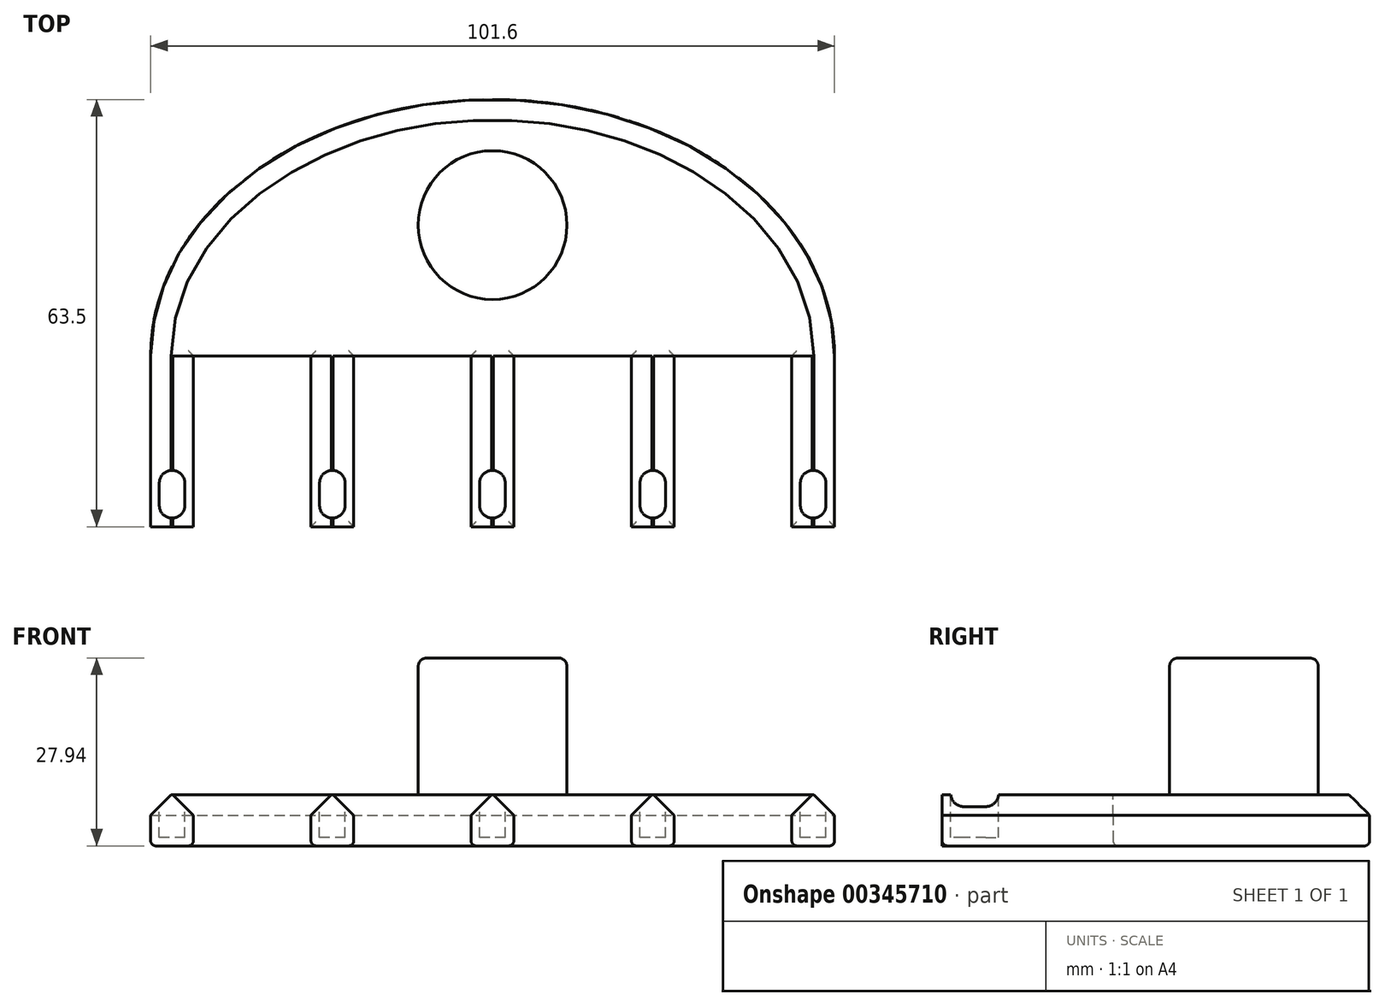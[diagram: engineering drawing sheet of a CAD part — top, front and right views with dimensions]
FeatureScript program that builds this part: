
annotation { "Feature Type Name" : "Feature", "Feature Type Description" : "" }
export const myFeature = defineFeature(function(context is Context, id is Id, definition is map)
    precondition{}
    {
        {
            var Q0;
            Q0=qCreatedBy(makeId("Top.planeOp"),FACE);
            var sketch = newSketch(context, id + "F0", { "sketchPlane" : qUnion([Q0])});
            skEllipticalArc(sketch, "E0", {});
            skPoint(sketch, "E1.end.orphan", {"position": v(-50.8, 0) * mm});
            skPoint(sketch, "E1.start.orphan", {"position": v(50.8, 0) * mm});
            skLineSegment(sketch, "E2", {"start": v(-50.8, 0) * mm, "end": v(-50.8, -25.4) * mm});
            skLineSegment(sketch, "E3", {"start": v(-50.8, -25.4) * mm, "end": v(-44.45, -25.4) * mm});
            skLineSegment(sketch, "E4", {"start": v(-44.45, -25.4) * mm, "end": v(-44.45, 0) * mm});
            skLineSegment(sketch, "E5", {"start": v(-44.45, 0) * mm, "end": v(-26.99, 0) * mm});
            skLineSegment(sketch, "E6", {"start": v(-26.99, 0) * mm, "end": v(-26.99, -25.4) * mm});
            skLineSegment(sketch, "E7", {"start": v(-26.99, -25.4) * mm, "end": v(-20.64, -25.4) * mm});
            skLineSegment(sketch, "E8", {"start": v(-20.64, -25.4) * mm, "end": v(-20.64, 0) * mm});
            skLineSegment(sketch, "E9", {"start": v(-20.64, 0) * mm, "end": v(-3.2, 0) * mm});
            skLineSegment(sketch, "E10", {"start": v(-3.2, 0) * mm, "end": v(-3.2, -25.4) * mm});
            skLineSegment(sketch, "E11", {"start": v(-3.2, -25.4) * mm, "end": v(3.15, -25.4) * mm});
            skLineSegment(sketch, "E12", {"start": v(3.15, -25.4) * mm, "end": v(3.15, 0) * mm});
            skLineSegment(sketch, "E13", {"start": v(3.15, 0) * mm, "end": v(20.62, 0) * mm});
            skLineSegment(sketch, "E14", {"start": v(20.62, 0) * mm, "end": v(20.62, -25.4) * mm});
            skLineSegment(sketch, "E15", {"start": v(20.62, -25.4) * mm, "end": v(26.97, -25.4) * mm});
            skLineSegment(sketch, "E16", {"start": v(26.97, -25.4) * mm, "end": v(26.97, 0) * mm});
            skLineSegment(sketch, "E17", {"start": v(26.97, 0) * mm, "end": v(44.45, 0) * mm});
            skLineSegment(sketch, "E18", {"start": v(44.45, 0) * mm, "end": v(44.45, -25.4) * mm});
            skLineSegment(sketch, "E19", {"start": v(44.45, -25.4) * mm, "end": v(50.8, -25.4) * mm});
            skLineSegment(sketch, "E20", {"start": v(50.8, -25.4) * mm, "end": v(50.8, 0) * mm});
            const initialGuessF0  = {"E0": [0, 0, 1, 0, 0.0508, 0.0381, 0, 3.141592653589793]};
            skSetInitialGuess(sketch, initialGuessF0);
            skSolve(sketch);
        }
        {
            var Q0;
            Q0=makeQuery(id+"F0.imprint","IMPRINT",FACE,{"disambiguationData":[TD([[makeQuery(id+"F0.imprint","IMPRINT",EDGE,{"derivedFrom":sQuery(id+"F0.wireOp",EDGE,"E0")}),1.0]])]});
            extrude(context, id + "F1", {"entities" : qUnion([Q0]), "depth" : 7.62 * mm});
        }
        {
            var Q0;
            Q0=makeQuery(id+"F1.opExtrude","CAP_FACE",FACE,{"disambiguationData":[OSD([sQuery(id+"F0.wireOp",EDGE,"E0"),sQuery(id+"F0.wireOp",EDGE,"soE1Z759-kknB-JbUd-iDBq-yKROK0KpcBBy")])],"isStart":false});
            var sketch = newSketch(context, id + "F2", { "sketchPlane" : qUnion([Q0])});
            skCircle(sketch, "E21", {"center": v(0, 19.43) * mm, "radius": 11.05 * mm});
            skSolve(sketch);
        }
        {
            var Q0;
            Q0=makeQuery(id+"F2.imprint","IMPRINT",FACE,{"disambiguationData":[TD([[makeQuery(id+"F2.imprint","IMPRINT",EDGE,{"derivedFrom":sQuery(id+"F2.wireOp",EDGE,"E21")}),1.0]])]});
            extrude(context, id + "F3", {"entities" : qUnion([Q0]), "operationType" : NewBodyOperationType.ADD, "depth" : 20.32 * mm});
        }
        {
            var Q0;
            Q0=makeQuery(id+"F1.opExtrude","CAP_FACE",FACE,{"disambiguationData":[OSD([sQuery(id+"F0.wireOp",EDGE,"E0"),sQuery(id+"F0.wireOp",EDGE,"E2"),sQuery(id+"F0.wireOp",EDGE,"E3"),sQuery(id+"F0.wireOp",EDGE,"E4"),sQuery(id+"F0.wireOp",EDGE,"E5"),sQuery(id+"F0.wireOp",EDGE,"E6"),sQuery(id+"F0.wireOp",EDGE,"E7"),sQuery(id+"F0.wireOp",EDGE,"E8"),sQuery(id+"F0.wireOp",EDGE,"E9"),sQuery(id+"F0.wireOp",EDGE,"E10"),sQuery(id+"F0.wireOp",EDGE,"E11"),sQuery(id+"F0.wireOp",EDGE,"E12"),sQuery(id+"F0.wireOp",EDGE,"E13"),sQuery(id+"F0.wireOp",EDGE,"E14"),sQuery(id+"F0.wireOp",EDGE,"E15"),sQuery(id+"F0.wireOp",EDGE,"E16"),sQuery(id+"F0.wireOp",EDGE,"E17"),sQuery(id+"F0.wireOp",EDGE,"E18"),sQuery(id+"F0.wireOp",EDGE,"E19"),sQuery(id+"F0.wireOp",EDGE,"E20")])],"isStart":false});
            var sketch = newSketch(context, id + "F4", { "sketchPlane" : qUnion([Q0])});
            skLineSegment(sketch, "E22", {"start": v(-49.53, -18.92) * mm, "end": v(-49.53, -22.23) * mm});
            skArc(sketch, "E23", {"start": v(-49.53, -22.23) * mm, "mid": v(-47.63, -24.13) * mm, "end": v(-45.72, -22.23) * mm});
            skLineSegment(sketch, "E24", {"start": v(-45.72, -22.23) * mm, "end": v(-45.72, -18.92) * mm});
            skArc(sketch, "E25", {"start": v(-49.53, -18.92) * mm, "mid": v(-47.63, -17.02) * mm, "end": v(-45.72, -18.92) * mm});
            skLineSegment(sketch, "E26", {"start": v(-25.72, -18.92) * mm, "end": v(-25.72, -22.23) * mm});
            skArc(sketch, "E27", {"start": v(-25.72, -22.23) * mm, "mid": v(-23.81, -24.13) * mm, "end": v(-21.9, -22.23) * mm});
            skLineSegment(sketch, "E28", {"start": v(-21.9, -22.23) * mm, "end": v(-21.9, -18.92) * mm});
            skArc(sketch, "E29", {"start": v(-25.72, -18.92) * mm, "mid": v(-23.81, -17.02) * mm, "end": v(-21.9, -18.92) * mm});
            skLineSegment(sketch, "E30", {"start": v(-1.93, -18.92) * mm, "end": v(-1.93, -22.23) * mm});
            skArc(sketch, "E31", {"start": v(-1.93, -22.23) * mm, "mid": v(-0.03, -24.13) * mm, "end": v(1.88, -22.23) * mm});
            skLineSegment(sketch, "E32", {"start": v(1.88, -22.23) * mm, "end": v(1.88, -18.92) * mm});
            skArc(sketch, "E33", {"start": v(-1.93, -18.92) * mm, "mid": v(-0.03, -17.02) * mm, "end": v(1.88, -18.92) * mm});
            skLineSegment(sketch, "E34", {"start": v(21.9, -18.92) * mm, "end": v(21.9, -22.23) * mm});
            skArc(sketch, "E35", {"start": v(21.9, -22.23) * mm, "mid": v(23.8, -24.13) * mm, "end": v(25.7, -22.23) * mm});
            skLineSegment(sketch, "E36", {"start": v(25.7, -22.23) * mm, "end": v(25.7, -18.92) * mm});
            skArc(sketch, "E37", {"start": v(21.9, -18.92) * mm, "mid": v(23.8, -17.02) * mm, "end": v(25.7, -18.92) * mm});
            skLineSegment(sketch, "E38", {"start": v(45.72, -18.92) * mm, "end": v(45.72, -22.22) * mm});
            skArc(sketch, "E39", {"start": v(45.72, -22.22) * mm, "mid": v(47.62, -24.13) * mm, "end": v(49.53, -22.22) * mm});
            skLineSegment(sketch, "E40", {"start": v(49.53, -22.22) * mm, "end": v(49.53, -18.92) * mm});
            skArc(sketch, "E41", {"start": v(45.72, -18.92) * mm, "mid": v(47.62, -17.02) * mm, "end": v(49.53, -18.92) * mm});
            skSolve(sketch);
        }
        {
            var Q0;
            Q0=makeQuery(id+"F4.imprint","IMPRINT",FACE,{"disambiguationData":[TD([[makeQuery(id+"F4.imprint","IMPRINT",EDGE,{"derivedFrom":sQuery(id+"F4.wireOp",EDGE,"E30")}),1.0]])]});
            var Q1;
            Q1=makeQuery(id+"F4.imprint","IMPRINT",FACE,{"disambiguationData":[TD([[makeQuery(id+"F4.imprint","IMPRINT",EDGE,{"derivedFrom":sQuery(id+"F4.wireOp",EDGE,"E34")}),1.0]])]});
            var Q2;
            Q2=makeQuery(id+"F4.imprint","IMPRINT",FACE,{"disambiguationData":[TD([[makeQuery(id+"F4.imprint","IMPRINT",EDGE,{"derivedFrom":sQuery(id+"F4.wireOp",EDGE,"E38")}),1.0]])]});
            var Q3;
            Q3=makeQuery(id+"F4.imprint","IMPRINT",FACE,{"disambiguationData":[TD([[makeQuery(id+"F4.imprint","IMPRINT",EDGE,{"derivedFrom":sQuery(id+"F4.wireOp",EDGE,"E26")}),1.0]])]});
            var Q4;
            Q4=makeQuery(id+"F4.imprint","IMPRINT",FACE,{"disambiguationData":[TD([[makeQuery(id+"F4.imprint","IMPRINT",EDGE,{"derivedFrom":sQuery(id+"F4.wireOp",EDGE,"E22")}),1.0]])]});
            extrude(context, id + "F5", {"entities" : qUnion([Q0, Q1, Q2, Q3, Q4]), "operationType" : NewBodyOperationType.REMOVE, "oppositeDirection" : true, "depth" : 6.35 * mm});
        }
        {
            var Q0;
            Q0=makeQuery(id+"F1.opExtrude","CAP_EDGE",EDGE,{"disambiguationData":[OSD([sQuery(id+"F0.wireOp",EDGE,"E2")])],"isStart":false});
            var Q1;
            Q1=makeQuery(id+"F1.opExtrude","CAP_EDGE",EDGE,{"disambiguationData":[OSD([sQuery(id+"F0.wireOp",EDGE,"E4")])],"isStart":false});
            var Q2;
            Q2=makeQuery(id+"F1.opExtrude","CAP_EDGE",EDGE,{"disambiguationData":[OSD([sQuery(id+"F0.wireOp",EDGE,"E6")])],"isStart":false});
            var Q3;
            Q3=makeQuery(id+"F1.opExtrude","CAP_EDGE",EDGE,{"disambiguationData":[OSD([sQuery(id+"F0.wireOp",EDGE,"E8")])],"isStart":false});
            var Q4;
            Q4=makeQuery(id+"F1.opExtrude","CAP_EDGE",EDGE,{"disambiguationData":[OSD([sQuery(id+"F0.wireOp",EDGE,"E10")])],"isStart":false});
            var Q5;
            Q5=makeQuery(id+"F1.opExtrude","CAP_EDGE",EDGE,{"disambiguationData":[OSD([sQuery(id+"F0.wireOp",EDGE,"E12")])],"isStart":false});
            var Q6;
            Q6=makeQuery(id+"F1.opExtrude","CAP_EDGE",EDGE,{"disambiguationData":[OSD([sQuery(id+"F0.wireOp",EDGE,"E14")])],"isStart":false});
            var Q7;
            Q7=makeQuery(id+"F1.opExtrude","CAP_EDGE",EDGE,{"disambiguationData":[OSD([sQuery(id+"F0.wireOp",EDGE,"E16")])],"isStart":false});
            var Q8;
            Q8=makeQuery(id+"F1.opExtrude","CAP_EDGE",EDGE,{"disambiguationData":[OSD([sQuery(id+"F0.wireOp",EDGE,"E18")])],"isStart":false});
            chamfer(context, id + "F6", {"entities" : qUnion([Q0, Q1, Q2, Q3, Q4, Q5, Q6, Q7, Q8]), "width" : 3.05 * mm, "tangentPropagation" : true});
        }
        {
            var Q0;
            Q0=makeQuery(id+"F1.opExtrude","CAP_EDGE",EDGE,{"disambiguationData":[OSD([sQuery(id+"F0.wireOp",EDGE,"E2")])],"isStart":true});
            var Q1;
            Q1=makeQuery(id+"F1.opExtrude","CAP_EDGE",EDGE,{"disambiguationData":[OSD([sQuery(id+"F0.wireOp",EDGE,"E4")])],"isStart":true});
            var Q2;
            Q2=makeQuery(id+"F1.opExtrude","CAP_EDGE",EDGE,{"disambiguationData":[OSD([sQuery(id+"F0.wireOp",EDGE,"E5")])],"isStart":true});
            var Q3;
            Q3=makeQuery(id+"F1.opExtrude","CAP_EDGE",EDGE,{"disambiguationData":[OSD([sQuery(id+"F0.wireOp",EDGE,"E6")])],"isStart":true});
            var Q4;
            Q4=makeQuery(id+"F1.opExtrude","CAP_EDGE",EDGE,{"disambiguationData":[OSD([sQuery(id+"F0.wireOp",EDGE,"E8")])],"isStart":true});
            var Q5;
            Q5=makeQuery(id+"F1.opExtrude","CAP_EDGE",EDGE,{"disambiguationData":[OSD([sQuery(id+"F0.wireOp",EDGE,"E7")])],"isStart":true});
            var Q6;
            Q6=makeQuery(id+"F1.opExtrude","CAP_EDGE",EDGE,{"disambiguationData":[OSD([sQuery(id+"F0.wireOp",EDGE,"E9")])],"isStart":true});
            var Q7;
            Q7=makeQuery(id+"F1.opExtrude","CAP_EDGE",EDGE,{"disambiguationData":[OSD([sQuery(id+"F0.wireOp",EDGE,"E10")])],"isStart":true});
            var Q8;
            Q8=makeQuery(id+"F1.opExtrude","CAP_EDGE",EDGE,{"disambiguationData":[OSD([sQuery(id+"F0.wireOp",EDGE,"E11")])],"isStart":true});
            var Q9;
            Q9=makeQuery(id+"F1.opExtrude","CAP_EDGE",EDGE,{"disambiguationData":[OSD([sQuery(id+"F0.wireOp",EDGE,"E12")])],"isStart":true});
            var Q10;
            Q10=makeQuery(id+"F1.opExtrude","CAP_EDGE",EDGE,{"disambiguationData":[OSD([sQuery(id+"F0.wireOp",EDGE,"E13")])],"isStart":true});
            var Q11;
            Q11=makeQuery(id+"F1.opExtrude","CAP_EDGE",EDGE,{"disambiguationData":[OSD([sQuery(id+"F0.wireOp",EDGE,"E14")])],"isStart":true});
            var Q12;
            Q12=makeQuery(id+"F1.opExtrude","CAP_EDGE",EDGE,{"disambiguationData":[OSD([sQuery(id+"F0.wireOp",EDGE,"E15")])],"isStart":true});
            var Q13;
            Q13=makeQuery(id+"F1.opExtrude","CAP_EDGE",EDGE,{"disambiguationData":[OSD([sQuery(id+"F0.wireOp",EDGE,"E16")])],"isStart":true});
            var Q14;
            Q14=makeQuery(id+"F1.opExtrude","CAP_EDGE",EDGE,{"disambiguationData":[OSD([sQuery(id+"F0.wireOp",EDGE,"E17")])],"isStart":true});
            var Q15;
            Q15=makeQuery(id+"F1.opExtrude","CAP_EDGE",EDGE,{"disambiguationData":[OSD([sQuery(id+"F0.wireOp",EDGE,"E18")])],"isStart":true});
            var Q16;
            Q16=makeQuery(id+"F1.opExtrude","CAP_EDGE",EDGE,{"disambiguationData":[OSD([sQuery(id+"F0.wireOp",EDGE,"E19")])],"isStart":true});
            fillet(context, id + "F7", {"entities" : qUnion([Q0, Q1, Q2, Q3, Q4, Q5, Q6, Q7, Q8, Q9, Q10, Q11, Q12, Q13, Q14, Q15, Q16]), "radius" : 0.76 * mm, "tangentPropagation" : true, "allowEdgeOverflow" : false});
        }
        {
            var Q0;
            Q0=makeQuery(id+"F3.opExtrude","CAP_EDGE",EDGE,{"disambiguationData":[OSD([sQuery(id+"F2.wireOp",EDGE,"E21")])],"isStart":false});
            fillet(context, id + "F8", {"entities" : qUnion([Q0]), "radius" : 1.27 * mm, "tangentPropagation" : true, "allowEdgeOverflow" : false});
        }
    });
